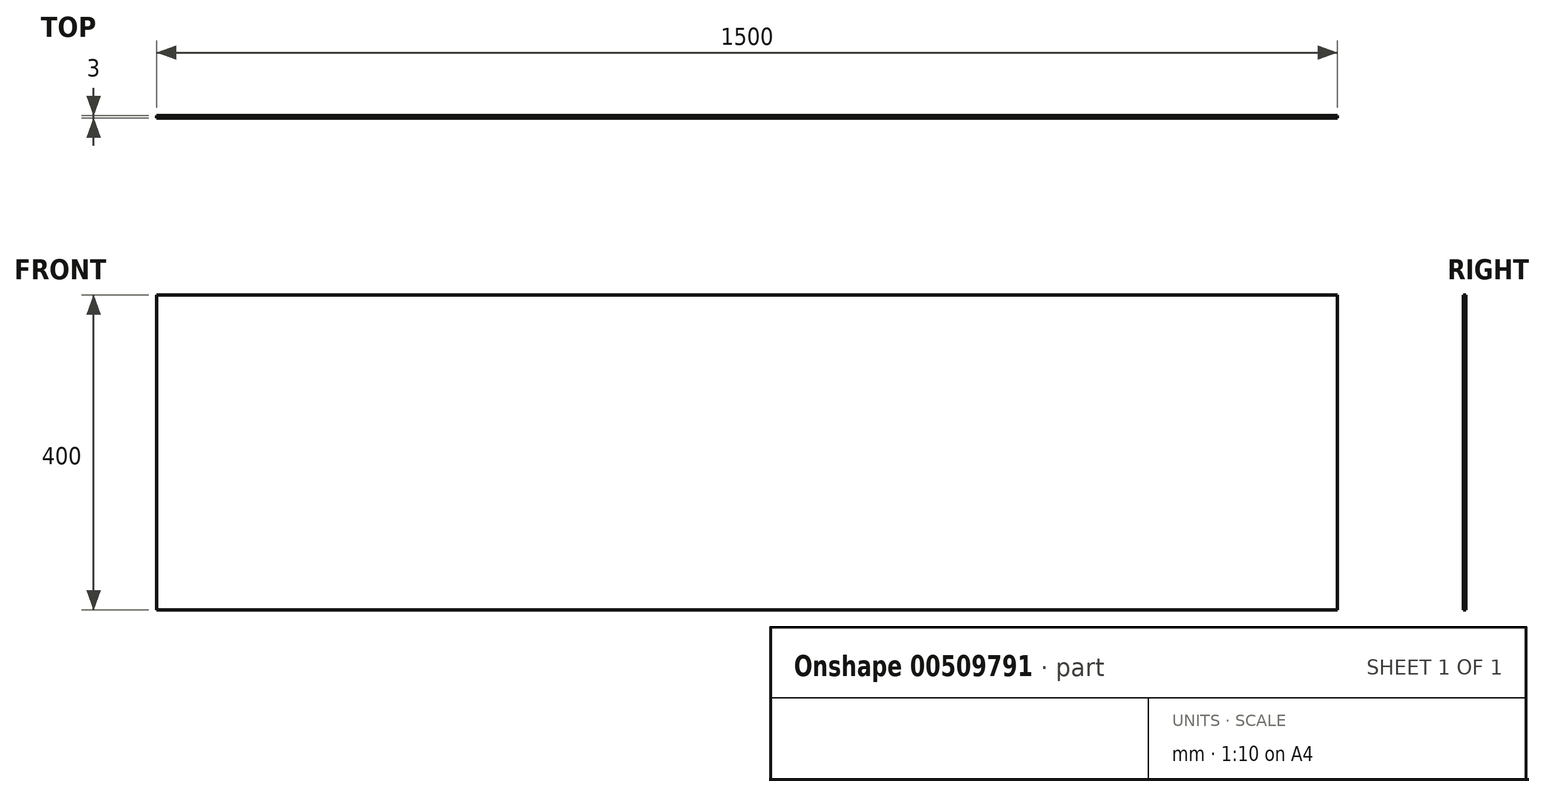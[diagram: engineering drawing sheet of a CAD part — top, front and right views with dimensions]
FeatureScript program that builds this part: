
annotation { "Feature Type Name" : "Feature", "Feature Type Description" : "" }
export const myFeature = defineFeature(function(context is Context, id is Id, definition is map)
    precondition{}
    {
        {
            var Q0;
            Q0=qCreatedBy(makeId("Front.planeOp"),FACE);
            var sketch = newSketch(context, id + "F0", { "sketchPlane" : qUnion([Q0])});
            skLineSegment(sketch, "E0.bottom", {"start": v(750, -200) * mm, "end": v(-750, -200) * mm});
            skLineSegment(sketch, "E0.top", {"start": v(750, 200) * mm, "end": v(-750, 200) * mm});
            skLineSegment(sketch, "E0.left", {"start": v(750, -200) * mm, "end": v(750, 200) * mm});
            skLineSegment(sketch, "E0.right", {"start": v(-750, -200) * mm, "end": v(-750, 200) * mm});
            skPoint(sketch, "E0.middle", {"position": v(0, 0) * mm});
            skSolve(sketch);
        }
        {
            var Q0;
            Q0 = qSketchRegion(id + "F0", true);
            extrude(context, id + "F1", {"entities" : qUnion([Q0]), "depth" : 3 * mm});
        }
    });
